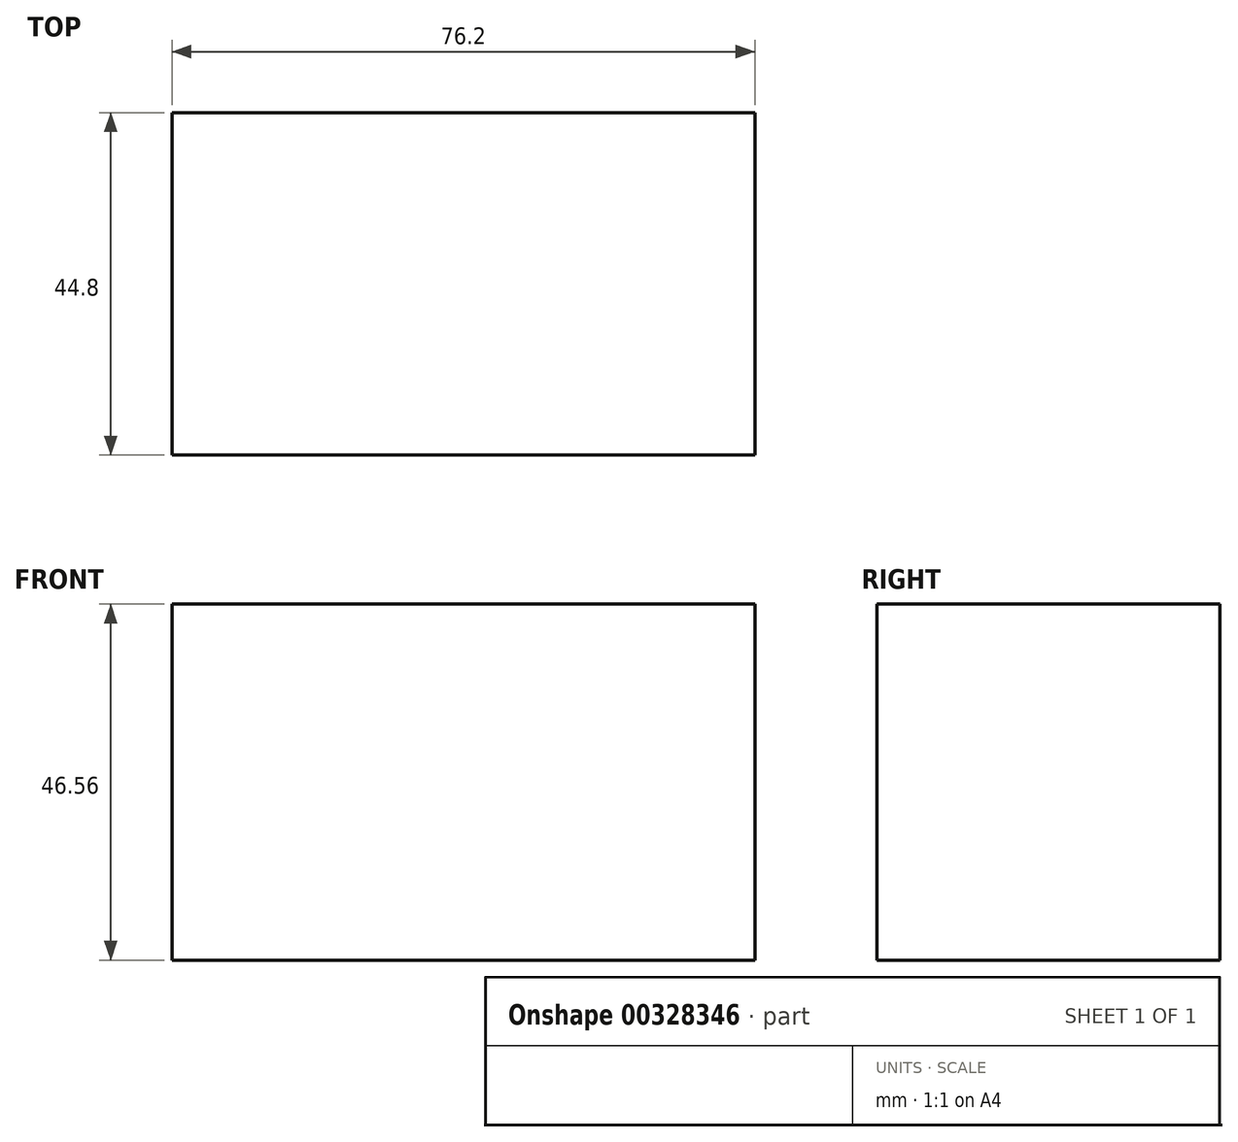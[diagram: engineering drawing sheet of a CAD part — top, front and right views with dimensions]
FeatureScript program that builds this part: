
annotation { "Feature Type Name" : "Feature", "Feature Type Description" : "" }
export const myFeature = defineFeature(function(context is Context, id is Id, definition is map)
    precondition{}
    {
        {
            var Q0;
            Q0=qCreatedBy(makeId("Right.planeOp"),FACE);
            var sketch = newSketch(context, id + "F0", { "sketchPlane" : qUnion([Q0])});
            skLineSegment(sketch, "E0.bottom", {"start": v(44.8, 0) * mm, "end": v(0, 0) * mm});
            skLineSegment(sketch, "E0.top", {"start": v(44.8, -46.56) * mm, "end": v(0, -46.56) * mm});
            skLineSegment(sketch, "E0.left", {"start": v(44.8, 0) * mm, "end": v(44.8, -46.56) * mm});
            skLineSegment(sketch, "E0.right", {"start": v(0, 0) * mm, "end": v(0, -46.56) * mm});
            skSolve(sketch);
        }
        {
            var Q0;
            Q0 = qSketchRegion(id + "F0", true);
            extrude(context, id + "F1", {"entities" : qUnion([Q0]), "depth" : 76.2 * mm});
        }
    });
